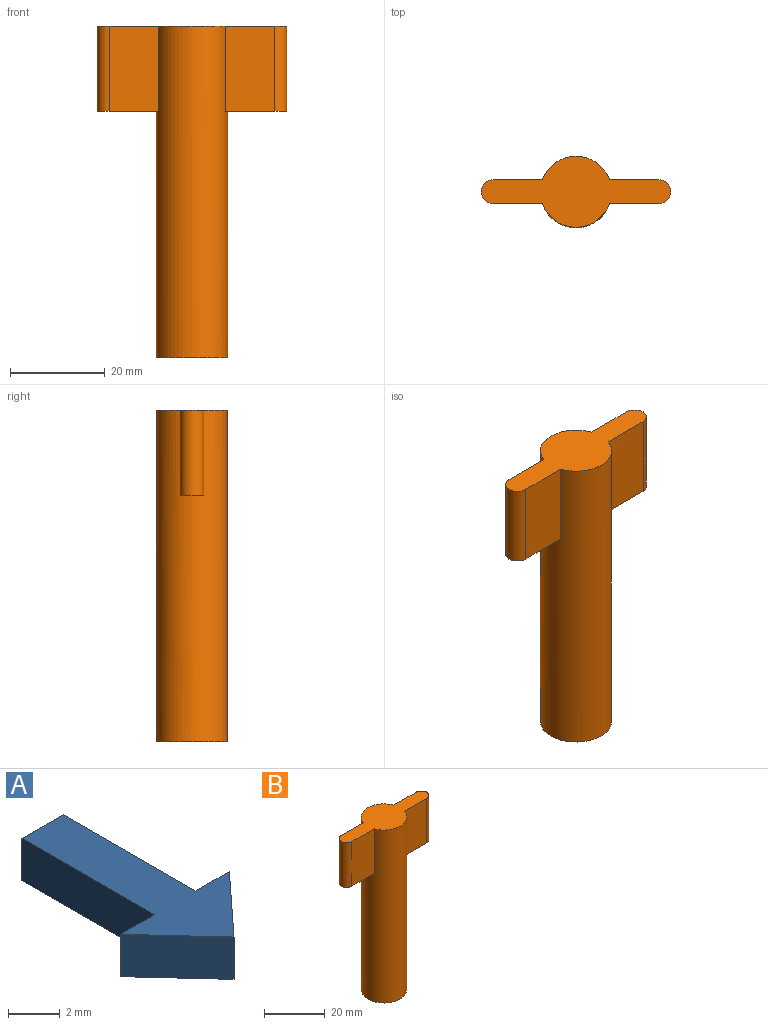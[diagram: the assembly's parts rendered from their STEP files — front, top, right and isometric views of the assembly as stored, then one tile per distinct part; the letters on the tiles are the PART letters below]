
ASSEMBLY  parts=2 mates=1
PART A: 9 faces, bbox 5.9x10.4x2 mm
  f0: plane 3.22x2.97mm, normal (-0.74,-0.68,0), area 8.8mm2, adj f1,f6,f7,f8
  f1: plane 2x1.85mm, normal (0,1,0), area 3.7mm2, adj f0,f2,f7,f8
  f2: plane 7.22x2mm, normal (-1,0,0), area 14.4mm2, adj f1,f3,f7,f8
  f3: plane 2.24x2mm, normal (0,1,0), area 4.5mm2, adj f2,f4,f7,f8
  f4: plane 7.22x2mm, normal (1,0,0), area 14.4mm2, adj f3,f5,f7,f8
  f5: plane 2x1.85mm, normal (0,1,0), area 3.7mm2, adj f4,f6,f7,f8
  f6: plane 3.22x2.97mm, normal (0.74,-0.68,0), area 8.8mm2, adj f0,f5,f7,f8
  f7: plane 10.45x5.94mm, normal (0,0,-1), area 25.8mm2, adj f0,f1,f2,f3,f4,f5,f6
  f8: plane 10.45x5.94mm, normal (0,0,1), area 25.8mm2, adj f0,f1,f2,f3,f4,f5,f6
PART B: 19 faces, bbox 40x15x70 mm
  f0: cylinder r=7.5mm len=70mm, axis (0,0,-1), area 3115.2mm2, adj f1,f2,f3,f4,f5,f6,f7,f8
  f1: plane 40x15mm, normal (0,0,1), area 297.8mm2, adj f0,f3,f4,f6,f7,f9,f10
  f2: plane 15x15mm, normal (0,0,-1), area 150.9mm2, adj f0,f11,f12,f13,f14,f15,f16,f17
  f3: plane 18x10.43mm, normal (0,-1,0), area 187.7mm2, adj f0,f1,f5,f9
  f4: plane 18x10.43mm, normal (0,1,0), area 187.7mm2, adj f0,f1,f5,f9
  f5: plane 12.93x5mm, normal (0,0,-1), area 60.5mm2, adj f0,f3,f4,f9
  f6: plane 18x10.43mm, normal (0,-1,0), area 187.7mm2, adj f0,f1,f8,f10
  f7: plane 18x10.43mm, normal (0,1,0), area 187.7mm2, adj f0,f1,f8,f10
  f8: plane 12.93x5mm, normal (0,0,-1), area 60.5mm2, adj f0,f6,f7,f10
  f9: cylinder r=2.5mm len=18mm, axis (0,0,1), area 141.4mm2, adj f1,f3,f4,f5
  f10: cylinder r=2.5mm len=18mm, axis (0,0,-1), area 141.4mm2, adj f1,f6,f7,f8
  f11: plane 3.22x2.97mm, normal (0.74,0.68,0), area 8.8mm2, adj f2,f12,f17,f18
  f12: plane 3.22x2.97mm, normal (-0.74,0.68,0), area 8.8mm2, adj f2,f11,f13,f18
  f13: plane 2x1.85mm, normal (0,-1,0), area 3.7mm2, adj f2,f12,f14,f18
  f14: plane 7.22x2mm, normal (-1,0,0), area 14.4mm2, adj f2,f13,f15,f18
  f15: plane 2.24x2mm, normal (0,-1,0), area 4.5mm2, adj f2,f14,f16,f18
  f16: plane 7.22x2mm, normal (1,0,0), area 14.4mm2, adj f2,f15,f17,f18
  f17: plane 2x1.85mm, normal (0,-1,0), area 3.7mm2, adj f2,f11,f16,f18
  f18: plane 10.45x5.94mm, normal (0,0,-1), area 25.8mm2, adj f11,f12,f13,f14,f15,f16,f17
PLACE A t=(9.04,6.34,-1.64)mm
PLACE B t=(9.04,6.34,-1.64)mm
MATE fastened B.f18 <-> A.f8  axis (0,0,-1) through (12.01,3.66,0.36)mm
